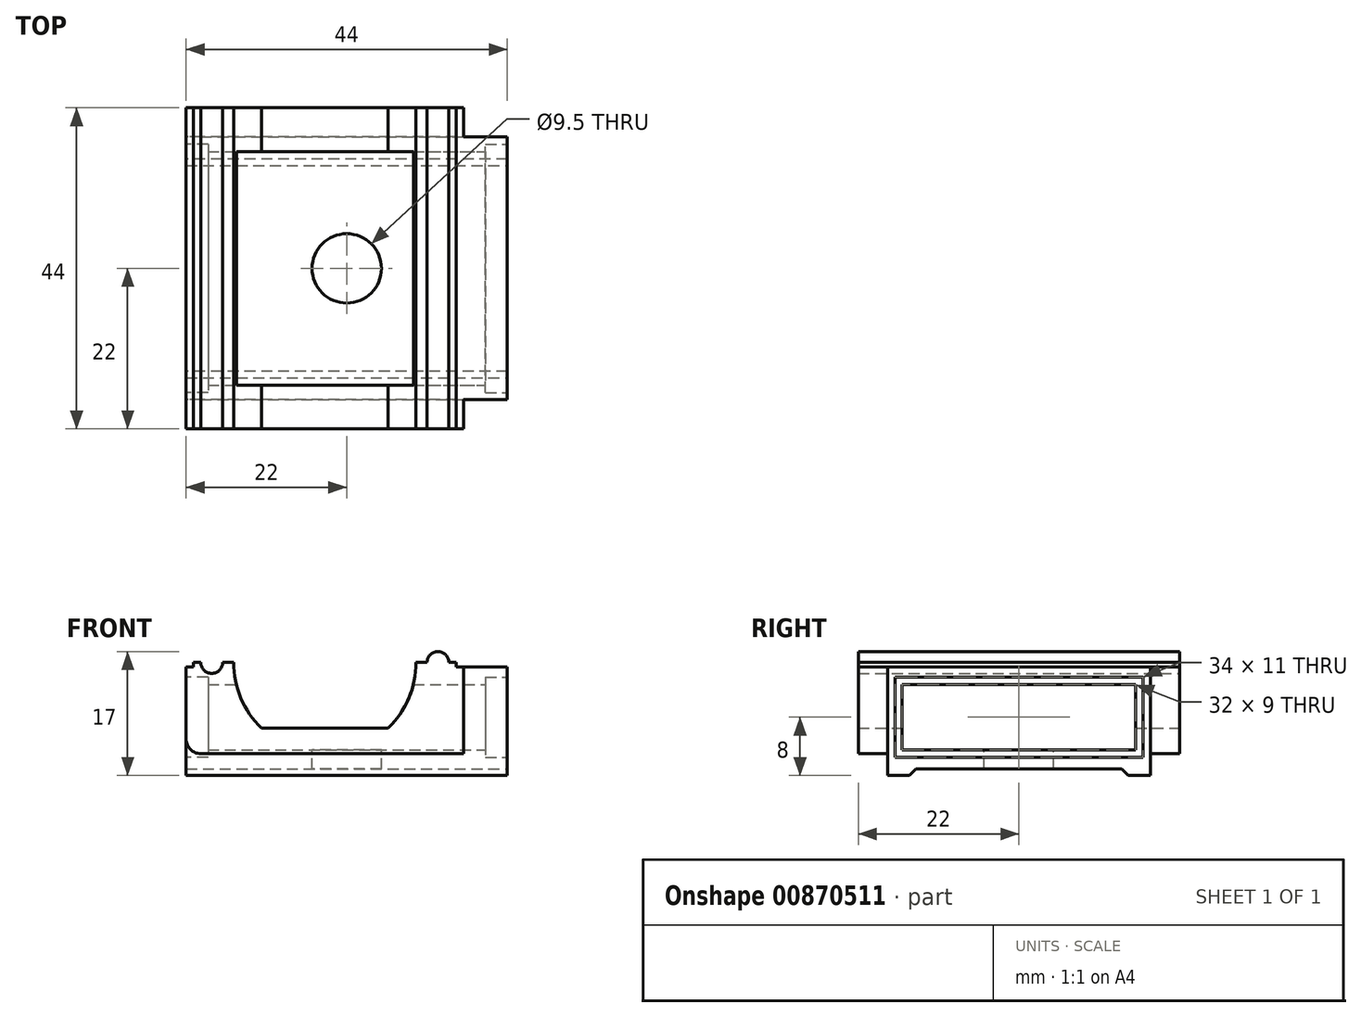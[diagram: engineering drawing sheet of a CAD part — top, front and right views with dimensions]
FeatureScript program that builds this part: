
annotation { "Feature Type Name" : "Feature", "Feature Type Description" : "" }
export const myFeature = defineFeature(function(context is Context, id is Id, definition is map)
    precondition{}
    {
        {
            var Q0;
            Q0=qCreatedBy(makeId("Top.planeOp"),FACE);
            var sketch = newSketch(context, id + "F0", { "sketchPlane" : qUnion([Q0])});
            skLineSegment(sketch, "E0.bottom", {"start": v(9.5, 19) * mm, "end": v(-9.5, 19) * mm});
            skLineSegment(sketch, "E0.top", {"start": v(9.5, -19) * mm, "end": v(-9.5, -19) * mm});
            skLineSegment(sketch, "E0.left", {"start": v(9.5, 19) * mm, "end": v(9.5, -19) * mm});
            skLineSegment(sketch, "E0.right", {"start": v(-9.5, 19) * mm, "end": v(-9.5, -19) * mm});
            skPoint(sketch, "E0.middle", {"position": v(0, 0) * mm});
            skLineSegment(sketch, "E1.bottom", {"start": v(-12.5, 22) * mm, "end": v(12.5, 22) * mm});
            skLineSegment(sketch, "E1.top", {"start": v(-12.5, -22) * mm, "end": v(12.5, -22) * mm});
            skLineSegment(sketch, "E1.left", {"start": v(-12.5, 22) * mm, "end": v(-12.5, -22) * mm});
            skLineSegment(sketch, "E1.right", {"start": v(12.5, 22) * mm, "end": v(12.5, -22) * mm});
            skCircle(sketch, "E2", {"center": v(3, 0) * mm, "radius": 4.75 * mm});
            skLineSegment(sketch, "E3.bottom", {"start": v(18.17, 25) * mm, "end": v(-18.17, 25) * mm});
            skLineSegment(sketch, "E3.top", {"start": v(18.17, -25) * mm, "end": v(-18.17, -25) * mm});
            skLineSegment(sketch, "E3.left", {"start": v(18.17, 25) * mm, "end": v(18.17, -25) * mm});
            skLineSegment(sketch, "E3.right", {"start": v(-18.17, 25) * mm, "end": v(-18.17, -25) * mm});
            skSolve(sketch);
        }
        {
            var Q0;
            Q0=qCreatedBy(makeId("Front.planeOp"),FACE);
            var sketch = newSketch(context, id + "F1", { "sketchPlane" : qUnion([Q0])});
            skCircle(sketch, "E4", {"center": v(0, 0) * mm, "radius": 9.5 * mm});
            skLineSegment(sketch, "E5.bottom", {"start": v(9.5, 6) * mm, "end": v(-9.5, 6) * mm});
            skLineSegment(sketch, "E5.top", {"start": v(9.5, -6) * mm, "end": v(-9.5, -6) * mm});
            skLineSegment(sketch, "E5.left", {"start": v(9.5, 6) * mm, "end": v(9.5, -6) * mm});
            skLineSegment(sketch, "E5.right", {"start": v(-9.5, 6) * mm, "end": v(-9.5, -6) * mm});
            skCircle(sketch, "E6", {"center": v(0, 0) * mm, "radius": 12.5 * mm});
            skLineSegment(sketch, "E7.bottom", {"start": v(-15.14, 9) * mm, "end": v(15.14, 9) * mm});
            skLineSegment(sketch, "E7.top", {"start": v(-15.14, -9) * mm, "end": v(15.14, -9) * mm});
            skLineSegment(sketch, "E7.left", {"start": v(-15.14, 9) * mm, "end": v(-15.14, -9) * mm});
            skLineSegment(sketch, "E7.right", {"start": v(15.14, 9) * mm, "end": v(15.14, -9) * mm});
            skLineSegment(sketch, "E8.bottom", {"start": v(-19, 12.6) * mm, "end": v(19, 12.6) * mm});
            skLineSegment(sketch, "E8.top", {"start": v(-19, -12.6) * mm, "end": v(19, -12.6) * mm});
            skLineSegment(sketch, "E8.left", {"start": v(-19, 12.6) * mm, "end": v(-19, -12.6) * mm});
            skLineSegment(sketch, "E8.right", {"start": v(19, 12.6) * mm, "end": v(19, -12.6) * mm});
            skCircle(sketch, "E9", {"center": v(0, 0) * mm, "radius": 15.5 * mm});
            skLineSegment(sketch, "E10", {"start": v(-15.14, 9) * mm, "end": v(-19, 9) * mm});
            skLineSegment(sketch, "E11", {"start": v(15.14, 9) * mm, "end": v(19, 9) * mm});
            skLineSegment(sketch, "E12", {"start": v(-15.14, -9) * mm, "end": v(-19, -9) * mm});
            skLineSegment(sketch, "E13", {"start": v(15.14, -9) * mm, "end": v(19, -9) * mm});
            skCircle(sketch, "E14", {"center": v(0, 0) * mm, "radius": 19 * mm});
            skLineSegment(sketch, "E15", {"start": v(-19, 0) * mm, "end": v(19, 0) * mm});
            skCircle(sketch, "E16", {"center": v(-15.5, 0) * mm, "radius": 1.5 * mm});
            skCircle(sketch, "E17", {"center": v(15.5, 0) * mm, "radius": 1.5 * mm});
            skLineSegment(sketch, "E18.bottom", {"start": v(-19, 0) * mm, "end": v(-18, 0) * mm});
            skLineSegment(sketch, "E18.top", {"start": v(-19, -0.6) * mm, "end": v(-18, -0.6) * mm});
            skLineSegment(sketch, "E18.left", {"start": v(-19, 0) * mm, "end": v(-19, -0.6) * mm});
            skLineSegment(sketch, "E18.right", {"start": v(-18, 0) * mm, "end": v(-18, -0.6) * mm});
            skLineSegment(sketch, "E19.bottom", {"start": v(19, 0) * mm, "end": v(18, 0) * mm});
            skLineSegment(sketch, "E19.top", {"start": v(19, -0.6) * mm, "end": v(18, -0.6) * mm});
            skLineSegment(sketch, "E19.left", {"start": v(19, 0) * mm, "end": v(19, -0.6) * mm});
            skLineSegment(sketch, "E19.right", {"start": v(18, 0) * mm, "end": v(18, -0.6) * mm});
            skLineSegment(sketch, "E20.top", {"start": v(-19, -14.6) * mm, "end": v(19, -14.6) * mm});
            skLineSegment(sketch, "E20.left", {"start": v(-19, -12.6) * mm, "end": v(-19, -14.6) * mm});
            skLineSegment(sketch, "E20.right", {"start": v(19, -12.6) * mm, "end": v(19, -14.6) * mm});
            skSolve(sketch);
        }
        {
            var Q0;
            Q0=qCreatedBy(makeId("Right.planeOp"),FACE);
            var sketch = newSketch(context, id + "F2", { "sketchPlane" : qUnion([Q0])});
            skLineSegment(sketch, "E21.bottom", {"start": v(-22, 12.5) * mm, "end": v(22, 12.5) * mm});
            skLineSegment(sketch, "E21.top", {"start": v(-22, -12.5) * mm, "end": v(22, -12.5) * mm});
            skLineSegment(sketch, "E21.left", {"start": v(-22, 12.5) * mm, "end": v(-22, -12.5) * mm});
            skLineSegment(sketch, "E21.right", {"start": v(22, 12.5) * mm, "end": v(22, -12.5) * mm});
            skPoint(sketch, "E21.middle", {"position": v(0, 0) * mm});
            skLineSegment(sketch, "E22.bottom", {"start": v(-18, -12.5) * mm, "end": v(-12, -12.5) * mm});
            skLineSegment(sketch, "E22.top", {"start": v(-18, -15.5) * mm, "end": v(-12, -15.5) * mm});
            skLineSegment(sketch, "E22.left", {"start": v(-18, -12.5) * mm, "end": v(-18, -15.5) * mm});
            skLineSegment(sketch, "E22.right", {"start": v(-12, -12.5) * mm, "end": v(-12, -15.5) * mm});
            skLineSegment(sketch, "E23.bottom", {"start": v(18, -12.5) * mm, "end": v(12, -12.5) * mm});
            skLineSegment(sketch, "E23.top", {"start": v(18, -15.5) * mm, "end": v(12, -15.5) * mm});
            skLineSegment(sketch, "E23.left", {"start": v(18, -12.5) * mm, "end": v(18, -15.5) * mm});
            skLineSegment(sketch, "E23.right", {"start": v(12, -12.5) * mm, "end": v(12, -15.5) * mm});
            skPoint(sketch, "E24.middle", {"position": v(0, -8.5) * mm});
            skLineSegment(sketch, "E25.bottom", {"start": v(18, -15.5) * mm, "end": v(22, -15.5) * mm});
            skLineSegment(sketch, "E25.top", {"start": v(18, -12.5) * mm, "end": v(22, -12.5) * mm});
            skLineSegment(sketch, "E25.left", {"start": v(18, -15.5) * mm, "end": v(18, -12.5) * mm});
            skLineSegment(sketch, "E25.right", {"start": v(22, -15.5) * mm, "end": v(22, -12.5) * mm});
            skLineSegment(sketch, "E26.bottom", {"start": v(-18, -15.5) * mm, "end": v(-22, -15.5) * mm});
            skLineSegment(sketch, "E26.top", {"start": v(-18, -12.5) * mm, "end": v(-22, -12.5) * mm});
            skLineSegment(sketch, "E26.left", {"start": v(-18, -15.5) * mm, "end": v(-18, -12.5) * mm});
            skLineSegment(sketch, "E26.right", {"start": v(-22, -15.5) * mm, "end": v(-22, -12.5) * mm});
            skSolve(sketch);
        }
        {
            var Q0;
            {var subQ4=sQuery(id+"F1.wireOp",EDGE,"E7.top");var subQ5=sQuery(id+"F1.wireOp",EDGE,"E6");var subQ6=makeQuery(id+"F1.imprint","INTERSECT",VERTEX,{"disambiguationData":[OD(0.0)],"derivedFrom":[subQ5,subQ4]});Q0=makeQuery(id+"F1.imprint","IMPRINT",FACE,{"disambiguationData":[TD([[makeQuery(id+"F1.imprint","IMPRINT",EDGE,{"disambiguationData":[TD([[subQ6,1.0]])],"derivedFrom":subQ5}),-1.0]])]});}
            var Q1;
            {var subQ0=sQuery(id+"F1.wireOp",EDGE,"E9");var subQ1=sQuery(id+"F1.wireOp",EDGE,"E7.top");var subQ2=makeQuery(id+"F1.imprint","INTERSECT",VERTEX,{"disambiguationData":[OD(0.0)],"derivedFrom":[subQ1,subQ0]});Q1=makeQuery(id+"F1.imprint","IMPRINT",FACE,{"disambiguationData":[TD([[makeQuery(id+"F1.imprint","IMPRINT",EDGE,{"disambiguationData":[TD([[subQ2,1.0]])],"derivedFrom":subQ0}),-1.0]])]});}
            var Q2;
            {var subQ0=sQuery(id+"F1.wireOp",EDGE,"E7.top");var subQ1=sQuery(id+"F1.wireOp",EDGE,"E4");var subQ2=makeQuery(id+"F1.imprint","INTERSECT",VERTEX,{"disambiguationData":[OD(0.0)],"derivedFrom":[subQ1,subQ0]});Q2=makeQuery(id+"F1.imprint","IMPRINT",FACE,{"disambiguationData":[TD([[makeQuery(id+"F1.imprint","IMPRINT",EDGE,{"disambiguationData":[TD([[subQ2,-1.0]])],"derivedFrom":subQ1}),-1.0]])]});}
            var Q3;
            {var subQ0=sQuery(id+"F1.wireOp",EDGE,"E7.right");var subQ3=sQuery(id+"F1.wireOp",EDGE,"E9");var subQ5=makeQuery(id+"F1.imprint","INTERSECT",VERTEX,{"disambiguationData":[OD(0.0)],"derivedFrom":[subQ0,subQ3]});Q3=makeQuery(id+"F1.imprint","IMPRINT",FACE,{"disambiguationData":[TD([[makeQuery(id+"F1.imprint","IMPRINT",EDGE,{"disambiguationData":[TD([[subQ5,1.0]])],"derivedFrom":subQ3}),-1.0]])]});}
            var Q4;
            {var subQ0=sQuery(id+"F1.wireOp",EDGE,"E8.right");var subQ1=sQuery(id+"F1.wireOp",EDGE,"E8.top");var subQ2=makeQuery(id+"F1.imprint","INTERSECT",VERTEX,{"derivedFrom":[subQ1,subQ0]});Q4=makeQuery(id+"F1.imprint","IMPRINT",FACE,{"disambiguationData":[TD([[makeQuery(id+"F1.imprint","IMPRINT",EDGE,{"disambiguationData":[TD([[subQ2,1.0]])],"derivedFrom":subQ1}),1.0]])]});}
            var Q5;
            {var subQ3=sQuery(id+"F1.wireOp",EDGE,"E14");var subQ7=sQuery(id+"F1.wireOp",EDGE,"E8.top");var subQ9=makeQuery(id+"F1.imprint","INTERSECT",VERTEX,{"disambiguationData":[OD(1.0)],"derivedFrom":[subQ7,subQ3]});Q5=makeQuery(id+"F1.imprint","IMPRINT",FACE,{"disambiguationData":[TD([[makeQuery(id+"F1.imprint","IMPRINT",EDGE,{"disambiguationData":[TD([[subQ9,1.0]])],"derivedFrom":subQ7}),1.0]])]});}
            var Q6;
            {var subQ3=sQuery(id+"F1.wireOp",EDGE,"E14");var subQ7=sQuery(id+"F1.wireOp",EDGE,"E8.top");var subQ9=makeQuery(id+"F1.imprint","INTERSECT",VERTEX,{"disambiguationData":[OD(0.0)],"derivedFrom":[subQ7,subQ3]});Q6=makeQuery(id+"F1.imprint","IMPRINT",FACE,{"disambiguationData":[TD([[makeQuery(id+"F1.imprint","IMPRINT",EDGE,{"disambiguationData":[TD([[subQ9,-1.0]])],"derivedFrom":subQ7}),1.0]])]});}
            var Q7;
            {var subQ0=sQuery(id+"F1.wireOp",EDGE,"E8.left");var subQ1=sQuery(id+"F1.wireOp",EDGE,"E8.top");var subQ2=makeQuery(id+"F1.imprint","INTERSECT",VERTEX,{"derivedFrom":[subQ1,subQ0]});Q7=makeQuery(id+"F1.imprint","IMPRINT",FACE,{"disambiguationData":[TD([[makeQuery(id+"F1.imprint","IMPRINT",EDGE,{"disambiguationData":[TD([[subQ2,-1.0]])],"derivedFrom":subQ1}),1.0]])]});}
            var Q8;
            {var subQ5=sQuery(id+"F1.wireOp",EDGE,"E18.right");Q8=makeQuery(id+"F1.imprint","IMPRINT",FACE,{"disambiguationData":[TD([[makeQuery(id+"F1.imprint","IMPRINT",EDGE,{"derivedFrom":subQ5}),1.0]])]});}
            var Q9;
            {var subQ7=sQuery(id+"F1.wireOp",EDGE,"E15");var subQ8=sQuery(id+"F1.wireOp",EDGE,"E6");var subQ9=makeQuery(id+"F1.imprint","INTERSECT",VERTEX,{"disambiguationData":[OD(1.0)],"derivedFrom":[subQ8,subQ7]});Q9=makeQuery(id+"F1.imprint","IMPRINT",FACE,{"disambiguationData":[TD([[makeQuery(id+"F1.imprint","IMPRINT",EDGE,{"disambiguationData":[TD([[subQ9,-1.0]])],"derivedFrom":subQ8}),-1.0]])]});}
            var Q10;
            {var subQ7=sQuery(id+"F1.wireOp",EDGE,"E6");var subQ9=sQuery(id+"F1.wireOp",EDGE,"E15");var subQ10=makeQuery(id+"F1.imprint","INTERSECT",VERTEX,{"disambiguationData":[OD(0.0)],"derivedFrom":[subQ7,subQ9]});Q10=makeQuery(id+"F1.imprint","IMPRINT",FACE,{"disambiguationData":[TD([[makeQuery(id+"F1.imprint","IMPRINT",EDGE,{"disambiguationData":[TD([[subQ10,1.0]])],"derivedFrom":subQ7}),-1.0]])]});}
            var Q11;
            {var subQ5=sQuery(id+"F1.wireOp",EDGE,"E19.right");Q11=makeQuery(id+"F1.imprint","IMPRINT",FACE,{"disambiguationData":[TD([[makeQuery(id+"F1.imprint","IMPRINT",EDGE,{"derivedFrom":subQ5}),-1.0]])]});}
            var Q12;
            {var subQ0=sQuery(id+"F1.wireOp",EDGE,"E17");var subQ1=sQuery(id+"F1.wireOp",EDGE,"E7.right");var subQ2=makeQuery(id+"F1.imprint","INTERSECT",VERTEX,{"disambiguationData":[OD(0.0)],"derivedFrom":[subQ1,subQ0]});Q12=makeQuery(id+"F1.imprint","IMPRINT",FACE,{"disambiguationData":[TD([[makeQuery(id+"F1.imprint","IMPRINT",EDGE,{"disambiguationData":[TD([[subQ2,1.0]])],"derivedFrom":subQ1}),1.0]])]});}
            var Q13;
            {var subQ0=sQuery(id+"F1.wireOp",EDGE,"E9");var subQ1=sQuery(id+"F1.wireOp",EDGE,"E7.left");var subQ2=makeQuery(id+"F1.imprint","INTERSECT",VERTEX,{"disambiguationData":[OD(1.0)],"derivedFrom":[subQ1,subQ0]});Q13=makeQuery(id+"F1.imprint","IMPRINT",FACE,{"disambiguationData":[TD([[makeQuery(id+"F1.imprint","IMPRINT",EDGE,{"disambiguationData":[TD([[subQ2,1.0]])],"derivedFrom":subQ1}),-1.0]])]});}
            var Q14;
            {var subQ0=sQuery(id+"F1.wireOp",EDGE,"E9");var subQ1=sQuery(id+"F1.wireOp",EDGE,"E7.right");var subQ2=makeQuery(id+"F1.imprint","INTERSECT",VERTEX,{"disambiguationData":[OD(0.0)],"derivedFrom":[subQ1,subQ0]});Q14=makeQuery(id+"F1.imprint","IMPRINT",FACE,{"disambiguationData":[TD([[makeQuery(id+"F1.imprint","IMPRINT",EDGE,{"disambiguationData":[TD([[subQ2,1.0]])],"derivedFrom":subQ1}),1.0]])]});}
            var Q15;
            {var subQ0=sQuery(id+"F1.wireOp",EDGE,"E17");var subQ1=sQuery(id+"F1.wireOp",EDGE,"E7.right");var subQ2=makeQuery(id+"F1.imprint","INTERSECT",VERTEX,{"disambiguationData":[OD(0.0)],"derivedFrom":[subQ1,subQ0]});Q15=makeQuery(id+"F1.imprint","IMPRINT",FACE,{"disambiguationData":[TD([[makeQuery(id+"F1.imprint","IMPRINT",EDGE,{"disambiguationData":[TD([[subQ2,1.0]])],"derivedFrom":subQ1}),-1.0]])]});}
            var Q16;
            {var subQ0=sQuery(id+"F1.wireOp",EDGE,"E15");var subQ1=sQuery(id+"F1.wireOp",EDGE,"E9");var subQ2=makeQuery(id+"F1.imprint","INTERSECT",VERTEX,{"disambiguationData":[OD(0.0)],"derivedFrom":[subQ1,subQ0]});Q16=makeQuery(id+"F1.imprint","IMPRINT",FACE,{"disambiguationData":[TD([[makeQuery(id+"F1.imprint","IMPRINT",EDGE,{"disambiguationData":[TD([[subQ2,1.0]])],"derivedFrom":subQ1}),-1.0]])]});}
            var Q17;
            {var subQ0=sQuery(id+"F1.wireOp",EDGE,"E15");var subQ1=sQuery(id+"F1.wireOp",EDGE,"E9");var subQ2=makeQuery(id+"F1.imprint","INTERSECT",VERTEX,{"disambiguationData":[OD(0.0)],"derivedFrom":[subQ1,subQ0]});Q17=makeQuery(id+"F1.imprint","IMPRINT",FACE,{"disambiguationData":[TD([[makeQuery(id+"F1.imprint","IMPRINT",EDGE,{"disambiguationData":[TD([[subQ2,-1.0]])],"derivedFrom":subQ1}),-1.0]])]});}
            var Q18;
            {var subQ0=sQuery(id+"F1.wireOp",EDGE,"E17");var subQ1=sQuery(id+"F1.wireOp",EDGE,"E7.right");var subQ2=makeQuery(id+"F1.imprint","INTERSECT",VERTEX,{"disambiguationData":[OD(1.0)],"derivedFrom":[subQ1,subQ0]});Q18=makeQuery(id+"F1.imprint","IMPRINT",FACE,{"disambiguationData":[TD([[makeQuery(id+"F1.imprint","IMPRINT",EDGE,{"disambiguationData":[TD([[subQ2,-1.0]])],"derivedFrom":subQ1}),1.0]])]});}
            var Q19;
            {var subQ0=sQuery(id+"F1.wireOp",EDGE,"E17");var subQ1=sQuery(id+"F1.wireOp",EDGE,"E7.right");var subQ2=makeQuery(id+"F1.imprint","INTERSECT",VERTEX,{"disambiguationData":[OD(1.0)],"derivedFrom":[subQ1,subQ0]});Q19=makeQuery(id+"F1.imprint","IMPRINT",FACE,{"disambiguationData":[TD([[makeQuery(id+"F1.imprint","IMPRINT",EDGE,{"disambiguationData":[TD([[subQ2,-1.0]])],"derivedFrom":subQ1}),-1.0]])]});}
            var Q20;
            {var subQ0=sQuery(id+"F1.wireOp",EDGE,"E7.top");var subQ1=sQuery(id+"F1.wireOp",EDGE,"E4");var subQ2=makeQuery(id+"F1.imprint","INTERSECT",VERTEX,{"disambiguationData":[OD(0.0)],"derivedFrom":[subQ1,subQ0]});Q20=makeQuery(id+"F1.imprint","IMPRINT",FACE,{"disambiguationData":[TD([[makeQuery(id+"F1.imprint","IMPRINT",EDGE,{"disambiguationData":[TD([[subQ2,-1.0]])],"derivedFrom":subQ1}),1.0]])]});}
            var Q21;
            {var subQ0=sQuery(id+"F1.wireOp",EDGE,"E18.top");var subQ1=sQuery(id+"F1.wireOp",EDGE,"E8.left");var subQ2=makeQuery(id+"F1.imprint","INTERSECT",VERTEX,{"derivedFrom":[subQ1,subQ0]});Q21=makeQuery(id+"F1.imprint","IMPRINT",FACE,{"disambiguationData":[TD([[makeQuery(id+"F1.imprint","IMPRINT",EDGE,{"disambiguationData":[TD([[subQ2,-1.0]])],"derivedFrom":subQ1}),1.0]])]});}
            var Q22;
            {var subQ0=sQuery(id+"F1.wireOp",EDGE,"E19.top");var subQ1=sQuery(id+"F1.wireOp",EDGE,"E8.right");var subQ2=makeQuery(id+"F1.imprint","INTERSECT",VERTEX,{"derivedFrom":[subQ1,subQ0]});Q22=makeQuery(id+"F1.imprint","IMPRINT",FACE,{"disambiguationData":[TD([[makeQuery(id+"F1.imprint","IMPRINT",EDGE,{"disambiguationData":[TD([[subQ2,-1.0]])],"derivedFrom":subQ1}),-1.0]])]});}
            var Q23;
            {var subQ5=sQuery(id+"F1.wireOp",EDGE,"E9");var subQ6=sQuery(id+"F1.wireOp",EDGE,"E8.top");var subQ7=makeQuery(id+"F1.imprint","INTERSECT",VERTEX,{"disambiguationData":[OD(0.0)],"derivedFrom":[subQ6,subQ5]});Q23=makeQuery(id+"F1.imprint","IMPRINT",FACE,{"disambiguationData":[TD([[makeQuery(id+"F1.imprint","IMPRINT",EDGE,{"disambiguationData":[TD([[subQ7,1.0]])],"derivedFrom":subQ6}),1.0]])]});}
            var Q24;
            {var subQ0=sQuery(id+"F1.wireOp",EDGE,"E14");var subQ5=sQuery(id+"F1.wireOp",EDGE,"E12");var subQ6=makeQuery(id+"F1.imprint","INTERSECT",VERTEX,{"derivedFrom":[subQ5,subQ0]});Q24=makeQuery(id+"F1.imprint","IMPRINT",FACE,{"disambiguationData":[TD([[makeQuery(id+"F1.imprint","IMPRINT",EDGE,{"disambiguationData":[TD([[subQ6,-1.0]])],"derivedFrom":subQ5}),1.0]])]});}
            var Q25;
            {var subQ5=sQuery(id+"F1.wireOp",EDGE,"E9");var subQ6=sQuery(id+"F1.wireOp",EDGE,"E8.top");var subQ7=makeQuery(id+"F1.imprint","INTERSECT",VERTEX,{"disambiguationData":[OD(1.0)],"derivedFrom":[subQ6,subQ5]});Q25=makeQuery(id+"F1.imprint","IMPRINT",FACE,{"disambiguationData":[TD([[makeQuery(id+"F1.imprint","IMPRINT",EDGE,{"disambiguationData":[TD([[subQ7,-1.0]])],"derivedFrom":subQ6}),1.0]])]});}
            var Q26;
            {var subQ3=sQuery(id+"F1.wireOp",EDGE,"E14");var subQ5=sQuery(id+"F1.wireOp",EDGE,"E13");var subQ7=makeQuery(id+"F1.imprint","INTERSECT",VERTEX,{"derivedFrom":[subQ5,subQ3]});Q26=makeQuery(id+"F1.imprint","IMPRINT",FACE,{"disambiguationData":[TD([[makeQuery(id+"F1.imprint","IMPRINT",EDGE,{"disambiguationData":[TD([[subQ7,-1.0]])],"derivedFrom":subQ5}),-1.0]])]});}
            var Q27;
            {var subQ3=sQuery(id+"F1.wireOp",EDGE,"E20.left");Q27=makeQuery(id+"F1.imprint","IMPRINT",FACE,{"disambiguationData":[TD([[makeQuery(id+"F1.imprint","IMPRINT",EDGE,{"derivedFrom":subQ3}),1.0]])]});}
            var Q28;
            {var subQ0=sQuery(id+"F1.wireOp",EDGE,"E9");var subQ1=sQuery(id+"F1.wireOp",EDGE,"E8.top");var subQ2=makeQuery(id+"F1.imprint","INTERSECT",VERTEX,{"disambiguationData":[OD(0.0)],"derivedFrom":[subQ1,subQ0]});Q28=makeQuery(id+"F1.imprint","IMPRINT",FACE,{"disambiguationData":[TD([[makeQuery(id+"F1.imprint","IMPRINT",EDGE,{"disambiguationData":[TD([[subQ2,1.0]])],"derivedFrom":subQ1}),-1.0]])]});}
            var Q29;
            {var subQ0=sQuery(id+"F1.wireOp",EDGE,"E9");var subQ1=sQuery(id+"F1.wireOp",EDGE,"E8.top");var subQ2=makeQuery(id+"F1.imprint","INTERSECT",VERTEX,{"disambiguationData":[OD(0.0)],"derivedFrom":[subQ1,subQ0]});Q29=makeQuery(id+"F1.imprint","IMPRINT",FACE,{"disambiguationData":[TD([[makeQuery(id+"F1.imprint","IMPRINT",EDGE,{"disambiguationData":[TD([[subQ2,-1.0]])],"derivedFrom":subQ1}),-1.0]])]});}
            var Q30;
            {var subQ0=sQuery(id+"F1.wireOp",EDGE,"E20.right");Q30=makeQuery(id+"F1.imprint","IMPRINT",FACE,{"disambiguationData":[TD([[makeQuery(id+"F1.imprint","IMPRINT",EDGE,{"derivedFrom":subQ0}),-1.0]])]});}
            var Q31;
            {var subQ0=sQuery(id+"F1.wireOp",EDGE,"E9");var subQ1=sQuery(id+"F1.wireOp",EDGE,"E8.top");var subQ2=makeQuery(id+"F1.imprint","INTERSECT",VERTEX,{"disambiguationData":[OD(1.0)],"derivedFrom":[subQ1,subQ0]});Q31=makeQuery(id+"F1.imprint","IMPRINT",FACE,{"disambiguationData":[TD([[makeQuery(id+"F1.imprint","IMPRINT",EDGE,{"disambiguationData":[TD([[subQ2,-1.0]])],"derivedFrom":subQ1}),-1.0]])]});}
            extrude(context, id + "F3", {"entities" : qUnion([Q0, Q1, Q2, Q3, Q4, Q5, Q6, Q7, Q8, Q9, Q10, Q11, Q12, Q13, Q14, Q15, Q16, Q17, Q18, Q19, Q20, Q21, Q22, Q23, Q24, Q25, Q26, Q27, Q28, Q29, Q30, Q31]), "endBound" : BoundingType.SYMMETRIC, "depth" : 44 * mm, "offsetDistance" : 25 * mm});
        }
        {
            var Q0;
            Q0=makeQuery(id+"F0.imprint","IMPRINT",FACE,{"disambiguationData":[TD([[makeQuery(id+"F0.imprint","IMPRINT",EDGE,{"derivedFrom":sQuery(id+"F0.wireOp",EDGE,"E2")}),1.0]])]});
            extrude(context, id + "F4", {"entities" : qUnion([Q0]), "operationType" : NewBodyOperationType.REMOVE, "oppositeDirection" : true, "depth" : 25 * mm, "offsetDistance" : 25 * mm});
        }
        {
            var Q0;
            Q0=makeQuery(id+"F2.imprint","IMPRINT",FACE,{"disambiguationData":[TD([[makeQuery(id+"F2.imprint","IMPRINT",EDGE,{"derivedFrom":sQuery(id+"F2.wireOp",EDGE,"E22.top")}),1.0]])]});
            var Q1;
            Q1=makeQuery(id+"F2.imprint","IMPRINT",FACE,{"disambiguationData":[TD([[makeQuery(id+"F2.imprint","IMPRINT",EDGE,{"derivedFrom":sQuery(id+"F2.wireOp",EDGE,"E23.top")}),-1.0]])]});
            extrude(context, id + "F5", {"entities" : qUnion([Q0, Q1]), "operationType" : NewBodyOperationType.ADD, "endBound" : BoundingType.SYMMETRIC, "depth" : 38 * mm, "offsetDistance" : 25 * mm});
        }
        {
            var Q0;
            Q0=makeQuery(id+"F3.opExtrude","SWEPT_FACE",FACE,{"disambiguationData":[OSD([sQuery(id+"F1.wireOp",EDGE,"E7.top")])]});
            var sketch = newSketch(context, id + "F6", { "sketchPlane" : qUnion([Q0])});
            skLineSegment(sketch, "E27.bottom", {"start": v(-27, 16) * mm, "end": v(33, 16) * mm});
            skLineSegment(sketch, "E27.top", {"start": v(-27, -16) * mm, "end": v(33, -16) * mm});
            skLineSegment(sketch, "E27.left", {"start": v(-27, 16) * mm, "end": v(-27, -16) * mm});
            skLineSegment(sketch, "E27.right", {"start": v(33, 16) * mm, "end": v(33, -16) * mm});
            skPoint(sketch, "E27.middle", {"position": v(3, 0) * mm});
            skSolve(sketch);
        }
        {
            var Q0;
            Q0 = qSketchRegion(id + "F6", true);
            extrude(context, id + "F7", {"entities" : qUnion([Q0]), "operationType" : NewBodyOperationType.REMOVE, "oppositeDirection" : true, "depth" : 3 * mm, "offsetDistance" : 25 * mm});
        }
        {
            var Q0;
            Q0 = qSketchRegion(id + "F6", true);
            extrude(context, id + "F8", {"entities" : qUnion([Q0]), "operationType" : NewBodyOperationType.REMOVE, "depth" : 3 * mm, "offsetDistance" : 25 * mm});
        }
        {
            var Q0;
            {var subQ2=sQuery(id+"F6.wireOp",EDGE,"E27.bottom");var subQ3=sQuery(id+"F6.wireOp",EDGE,"E27.top");Q0=makeQuery(id+"F8.boolean.opBoolean","COPY",FACE,{"disambiguationData":[TD([makeQuery(id+"F3.opExtrude","SWEPT_FACE",FACE,{"disambiguationData":[OSD([sQuery(id+"F1.wireOp",EDGE,"E8.left"),sQuery(id+"F1.wireOp",EDGE,"E20.left")])]})])],"derivedFrom":makeQuery(id+"F8.opExtrude","CAP_FACE",FACE,{"disambiguationData":[OSD([subQ2,subQ3,sQuery(id+"F6.wireOp",EDGE,"E27.left"),sQuery(id+"F6.wireOp",EDGE,"E27.right")])],"isStart":false})});}
            extrude(context, id + "F9", {"entities" : qUnion([Q0]), "operationType" : NewBodyOperationType.REMOVE, "oppositeDirection" : true, "depth" : 3 * mm, "offsetDistance" : 25 * mm});
        }
        {
            var Q0;
            {var subQ1=sQuery(id+"F6.wireOp",EDGE,"E27.top");var subQ2=sQuery(id+"F6.wireOp",EDGE,"E27.bottom");Q0=makeQuery(id+"F8.boolean.opBoolean","COPY",FACE,{"disambiguationData":[TD([makeQuery(id+"F3.opExtrude","SWEPT_FACE",FACE,{"disambiguationData":[OSD([sQuery(id+"F1.wireOp",EDGE,"E8.right"),sQuery(id+"F1.wireOp",EDGE,"E20.right")])]})])],"derivedFrom":makeQuery(id+"F8.opExtrude","CAP_FACE",FACE,{"disambiguationData":[OSD([subQ2,subQ1,sQuery(id+"F6.wireOp",EDGE,"E27.left"),sQuery(id+"F6.wireOp",EDGE,"E27.right")])],"isStart":false})});}
            extrude(context, id + "F10", {"entities" : qUnion([Q0]), "operationType" : NewBodyOperationType.REMOVE, "oppositeDirection" : true, "depth" : 3 * mm, "offsetDistance" : 25 * mm});
        }
        {
            var Q0;
            {var subQ0=sQuery(id+"F2.wireOp",EDGE,"E21.top");Q0=makeQuery(id+"F5.boolean.opBoolean","MERGE",FACE,{"derivedFrom":[makeQuery(id+"F3.opExtrude","SWEPT_FACE",FACE,{"disambiguationData":[OSD([sQuery(id+"F1.wireOp",EDGE,"E8.right"),sQuery(id+"F1.wireOp",EDGE,"E20.right")])]}),makeQuery(id+"F5.opExtrude","CAP_FACE",FACE,{"disambiguationData":[OSD([subQ0,sQuery(id+"F2.wireOp",EDGE,"E23.top"),sQuery(id+"F2.wireOp",EDGE,"E23.left"),sQuery(id+"F2.wireOp",EDGE,"E23.right")])],"isStart":false}),makeQuery(id+"F5.opExtrude","CAP_FACE",FACE,{"disambiguationData":[OSD([subQ0,sQuery(id+"F2.wireOp",EDGE,"E22.top"),sQuery(id+"F2.wireOp",EDGE,"E22.left"),sQuery(id+"F2.wireOp",EDGE,"E22.right")])],"isStart":false})]});}
            extrude(context, id + "F11", {"entities" : qUnion([Q0]), "operationType" : NewBodyOperationType.ADD, "depth" : 6 * mm, "offsetDistance" : 25 * mm});
        }
        {
            var Q0;
            Q0=makeQuery(id+"F11.opExtrude","CAP_FACE",FACE,{"disambiguationData":[OSD([sQuery(id+"F1.wireOp",EDGE,"E8.right"),sQuery(id+"F1.wireOp",EDGE,"E20.right"),sQuery(id+"F2.wireOp",EDGE,"E21.top"),sQuery(id+"F2.wireOp",EDGE,"E22.top"),sQuery(id+"F2.wireOp",EDGE,"E22.left"),sQuery(id+"F2.wireOp",EDGE,"E22.right"),sQuery(id+"F2.wireOp",EDGE,"E23.top"),sQuery(id+"F2.wireOp",EDGE,"E23.left"),sQuery(id+"F2.wireOp",EDGE,"E23.right")])],"isStart":false});
            var sketch = newSketch(context, id + "F12", { "sketchPlane" : qUnion([Q0])});
            skLineSegment(sketch, "E28.bottom", {"start": v(-17, -2) * mm, "end": v(17, -2) * mm});
            skLineSegment(sketch, "E28.top", {"start": v(-17, -13) * mm, "end": v(17, -13) * mm});
            skLineSegment(sketch, "E28.left", {"start": v(-17, -2) * mm, "end": v(-17, -13) * mm});
            skLineSegment(sketch, "E28.right", {"start": v(17, -2) * mm, "end": v(17, -13) * mm});
            skSolve(sketch);
        }
        {
            var Q0;
            Q0=makeQuery(id+"F12.imprint","IMPRINT",FACE,{"disambiguationData":[TD([[makeQuery(id+"F12.imprint","IMPRINT",EDGE,{"derivedFrom":sQuery(id+"F12.wireOp",EDGE,"E28.bottom")}),-1.0]])]});
            extrude(context, id + "F13", {"entities" : qUnion([Q0]), "operationType" : NewBodyOperationType.REMOVE, "oppositeDirection" : true, "depth" : 3 * mm, "offsetDistance" : 25 * mm});
        }
        {
            var Q0;
            {var subQ0=sQuery(id+"F2.wireOp",EDGE,"E21.top");Q0=makeQuery(id+"F5.boolean.opBoolean","MERGE",FACE,{"derivedFrom":[makeQuery(id+"F3.opExtrude","SWEPT_FACE",FACE,{"disambiguationData":[OSD([sQuery(id+"F1.wireOp",EDGE,"E8.left"),sQuery(id+"F1.wireOp",EDGE,"E20.left")])]}),makeQuery(id+"F5.opExtrude","CAP_FACE",FACE,{"disambiguationData":[OSD([subQ0,sQuery(id+"F2.wireOp",EDGE,"E23.top"),sQuery(id+"F2.wireOp",EDGE,"E23.left"),sQuery(id+"F2.wireOp",EDGE,"E23.right")])],"isStart":true}),makeQuery(id+"F5.opExtrude","CAP_FACE",FACE,{"disambiguationData":[OSD([subQ0,sQuery(id+"F2.wireOp",EDGE,"E22.top"),sQuery(id+"F2.wireOp",EDGE,"E22.left"),sQuery(id+"F2.wireOp",EDGE,"E22.right")])],"isStart":true})]});}
            var sketch = newSketch(context, id + "F14", { "sketchPlane" : qUnion([Q0])});
            skLineSegment(sketch, "E29.bottom", {"start": v(-17, -2) * mm, "end": v(17, -2) * mm});
            skLineSegment(sketch, "E29.top", {"start": v(-17, -13) * mm, "end": v(17, -13) * mm});
            skLineSegment(sketch, "E29.left", {"start": v(-17, -2) * mm, "end": v(-17, -13) * mm});
            skLineSegment(sketch, "E29.right", {"start": v(17, -2) * mm, "end": v(17, -13) * mm});
            skSolve(sketch);
        }
        {
            var Q0;
            Q0=makeQuery(id+"F14.imprint","IMPRINT",FACE,{"disambiguationData":[TD([[makeQuery(id+"F14.imprint","IMPRINT",EDGE,{"derivedFrom":sQuery(id+"F14.wireOp",EDGE,"E29.bottom")}),-1.0]])]});
            extrude(context, id + "F15", {"entities" : qUnion([Q0]), "operationType" : NewBodyOperationType.REMOVE, "oppositeDirection" : true, "depth" : 3 * mm, "offsetDistance" : 25 * mm});
        }
        {
            var Q0;
            {var subQ2=sQuery(id+"F2.wireOp",EDGE,"E23.left");Q0=makeQuery(id+"F2.imprint","IMPRINT",FACE,{"disambiguationData":[TD([[makeQuery(id+"F2.imprint","IMPRINT",EDGE,{"derivedFrom":subQ2}),1.0]])]});}
            var Q1;
            {var subQ0=sQuery(id+"F2.wireOp",EDGE,"E22.left");Q1=makeQuery(id+"F2.imprint","IMPRINT",FACE,{"disambiguationData":[TD([[makeQuery(id+"F2.imprint","IMPRINT",EDGE,{"derivedFrom":subQ0}),-1.0]])]});}
            extrude(context, id + "F16", {"entities" : qUnion([Q0, Q1]), "operationType" : NewBodyOperationType.REMOVE, "endBound" : BoundingType.SYMMETRIC, "oppositeDirection" : true, "depth" : 50 * mm, "offsetDistance" : 25 * mm});
        }
        {
            var Q0;
            {var subQ0=sQuery(id+"F2.wireOp",EDGE,"E23.right");var subQ1=sQuery(id+"F2.wireOp",EDGE,"E23.top");Q0=makeQuery(id+"F11.boolean.opBoolean","MERGE",EDGE,{"derivedFrom":[makeQuery(id+"F5.opExtrude","SWEPT_EDGE",EDGE,{"disambiguationData":[OSD([subQ1,subQ0])]}),makeQuery(id+"F11.opExtrude","SWEPT_EDGE",EDGE,{"disambiguationData":[OSD([subQ1,subQ0])]})]});}
            var Q1;
            {var subQ0=sQuery(id+"F2.wireOp",EDGE,"E22.right");var subQ1=sQuery(id+"F2.wireOp",EDGE,"E22.top");Q1=makeQuery(id+"F11.boolean.opBoolean","MERGE",EDGE,{"derivedFrom":[makeQuery(id+"F5.opExtrude","SWEPT_EDGE",EDGE,{"disambiguationData":[OSD([subQ1,subQ0])]}),makeQuery(id+"F11.opExtrude","SWEPT_EDGE",EDGE,{"disambiguationData":[OSD([subQ1,subQ0])]})]});}
            chamfer(context, id + "F17", {"entities" : qUnion([Q0, Q1]), "width" : 3 * mm, "tangentPropagation" : true});
        }
        {
            var Q0;
            {var subQ0=sQuery(id+"F1.wireOp",EDGE,"E20.right");var subQ1=sQuery(id+"F1.wireOp",EDGE,"E8.right");Q0=makeQuery(id+"F11.boolean.opBoolean","MERGE",FACE,{"derivedFrom":[makeQuery(id+"F3.opExtrude","CAP_FACE",FACE,{"disambiguationData":[OSD([sQuery(id+"F1.wireOp",EDGE,"E6"),sQuery(id+"F1.wireOp",EDGE,"E7.top"),sQuery(id+"F1.wireOp",EDGE,"E8.left"),subQ1,sQuery(id+"F1.wireOp",EDGE,"E15"),sQuery(id+"F1.wireOp",EDGE,"E16"),sQuery(id+"F1.wireOp",EDGE,"E17"),sQuery(id+"F1.wireOp",EDGE,"E18.top"),sQuery(id+"F1.wireOp",EDGE,"E18.right"),sQuery(id+"F1.wireOp",EDGE,"E19.top"),sQuery(id+"F1.wireOp",EDGE,"E19.right"),sQuery(id+"F1.wireOp",EDGE,"E20.top"),sQuery(id+"F1.wireOp",EDGE,"E20.left"),subQ0])],"isStart":false}),makeQuery(id+"F11.opExtrude","SWEPT_FACE",FACE,{"disambiguationData":[OSD([subQ1,subQ0]),TDD([makeQuery(id+"F3.opExtrude","CAP_EDGE",EDGE,{"disambiguationData":[OSD([subQ1,subQ0])],"isStart":false})])]})]});}
            var sketch = newSketch(context, id + "F18", { "sketchPlane" : qUnion([Q0])});
            skLineSegment(sketch, "E30.bottom", {"start": v(25, -12.5) * mm, "end": v(19, -12.5) * mm});
            skLineSegment(sketch, "E30.top", {"start": v(25, -0.6) * mm, "end": v(19, -0.6) * mm});
            skLineSegment(sketch, "E30.left", {"start": v(25, -12.5) * mm, "end": v(25, -0.6) * mm});
            skLineSegment(sketch, "E30.right", {"start": v(19, -12.5) * mm, "end": v(19, -0.6) * mm});
            skSolve(sketch);
        }
        {
            var Q0;
            Q0=makeQuery(id+"F18.imprint","IMPRINT",FACE,{"disambiguationData":[TD([[makeQuery(id+"F18.imprint","IMPRINT",EDGE,{"derivedFrom":sQuery(id+"F18.wireOp",EDGE,"E30.bottom")}),1.0]])]});
            extrude(context, id + "F19", {"entities" : qUnion([Q0]), "operationType" : NewBodyOperationType.REMOVE, "oppositeDirection" : true, "depth" : 4 * mm, "offsetDistance" : 25 * mm});
        }
        {
            var Q0;
            {var subQ0=sQuery(id+"F1.wireOp",EDGE,"E20.right");var subQ1=sQuery(id+"F1.wireOp",EDGE,"E8.right");Q0=makeQuery(id+"F11.boolean.opBoolean","MERGE",FACE,{"derivedFrom":[makeQuery(id+"F3.opExtrude","CAP_FACE",FACE,{"disambiguationData":[OSD([sQuery(id+"F1.wireOp",EDGE,"E6"),sQuery(id+"F1.wireOp",EDGE,"E7.top"),sQuery(id+"F1.wireOp",EDGE,"E8.left"),subQ1,sQuery(id+"F1.wireOp",EDGE,"E15"),sQuery(id+"F1.wireOp",EDGE,"E16"),sQuery(id+"F1.wireOp",EDGE,"E17"),sQuery(id+"F1.wireOp",EDGE,"E18.top"),sQuery(id+"F1.wireOp",EDGE,"E18.right"),sQuery(id+"F1.wireOp",EDGE,"E19.top"),sQuery(id+"F1.wireOp",EDGE,"E19.right"),sQuery(id+"F1.wireOp",EDGE,"E20.top"),sQuery(id+"F1.wireOp",EDGE,"E20.left"),subQ0])],"isStart":true}),makeQuery(id+"F11.opExtrude","SWEPT_FACE",FACE,{"disambiguationData":[OSD([subQ1,subQ0]),TDD([makeQuery(id+"F3.opExtrude","CAP_EDGE",EDGE,{"disambiguationData":[OSD([subQ1,subQ0])],"isStart":true})])]})]});}
            var sketch = newSketch(context, id + "F20", { "sketchPlane" : qUnion([Q0])});
            skLineSegment(sketch, "E31.bottom", {"start": v(-25, -12.5) * mm, "end": v(-19, -12.5) * mm});
            skLineSegment(sketch, "E31.top", {"start": v(-25, -0.6) * mm, "end": v(-19, -0.6) * mm});
            skLineSegment(sketch, "E31.left", {"start": v(-25, -12.5) * mm, "end": v(-25, -0.6) * mm});
            skLineSegment(sketch, "E31.right", {"start": v(-19, -12.5) * mm, "end": v(-19, -0.6) * mm});
            skSolve(sketch);
        }
        {
            var Q0;
            Q0=makeQuery(id+"F20.imprint","IMPRINT",FACE,{"disambiguationData":[TD([[makeQuery(id+"F20.imprint","IMPRINT",EDGE,{"derivedFrom":sQuery(id+"F20.wireOp",EDGE,"E31.bottom")}),-1.0]])]});
            extrude(context, id + "F21", {"entities" : qUnion([Q0]), "operationType" : NewBodyOperationType.REMOVE, "oppositeDirection" : true, "depth" : 4 * mm, "offsetDistance" : 25 * mm});
        }
        {
            var Q0;
            {var subQ0=sQuery(id+"F2.wireOp",EDGE,"E21.top");var subQ1=sQuery(id+"F2.wireOp",EDGE,"E23.left");Q0=makeQuery(id+"F16.boolean.opBoolean","INTERSECT",EDGE,{"derivedFrom":[makeQuery(id+"F5.boolean.opBoolean","MERGE",FACE,{"derivedFrom":[makeQuery(id+"F3.opExtrude","SWEPT_FACE",FACE,{"disambiguationData":[OSD([sQuery(id+"F1.wireOp",EDGE,"E8.left"),sQuery(id+"F1.wireOp",EDGE,"E20.left")])]}),makeQuery(id+"F5.opExtrude","CAP_FACE",FACE,{"disambiguationData":[OSD([subQ0,sQuery(id+"F2.wireOp",EDGE,"E23.top"),subQ1,sQuery(id+"F2.wireOp",EDGE,"E23.right")])],"isStart":true}),makeQuery(id+"F5.opExtrude","CAP_FACE",FACE,{"disambiguationData":[OSD([subQ0,sQuery(id+"F2.wireOp",EDGE,"E22.top"),sQuery(id+"F2.wireOp",EDGE,"E22.left"),sQuery(id+"F2.wireOp",EDGE,"E22.right")])],"isStart":true})]}),makeQuery(id+"F16.opExtrude","SWEPT_FACE",FACE,{"disambiguationData":[OSD([subQ0]),TDD([makeQuery(id+"F2.imprint","IMPRINT",EDGE,{"disambiguationData":[TD([[makeQuery(id+"F2.imprint","INTERSECT",VERTEX,{"derivedFrom":[subQ0,subQ1]}),-1.0]])],"derivedFrom":subQ0})])]})]});}
            var Q1;
            Q1=makeQuery(id+"F19.boolean.opBoolean","COPY",EDGE,{"derivedFrom":makeQuery(id+"F19.opExtrude","SWEPT_EDGE",EDGE,{"disambiguationData":[OSD([sQuery(id+"F2.wireOp",EDGE,"E21.top"),sQuery(id+"F2.wireOp",EDGE,"E21.left"),sQuery(id+"F2.wireOp",EDGE,"E26.right"),sQuery(id+"F18.wireOp",EDGE,"E30.bottom"),sQuery(id+"F18.wireOp",EDGE,"E30.right")])]})});
            var Q2;
            Q2=makeQuery(id+"F21.boolean.opBoolean","COPY",EDGE,{"derivedFrom":makeQuery(id+"F21.opExtrude","SWEPT_EDGE",EDGE,{"disambiguationData":[OSD([sQuery(id+"F2.wireOp",EDGE,"E21.top"),sQuery(id+"F2.wireOp",EDGE,"E21.right"),sQuery(id+"F2.wireOp",EDGE,"E25.right"),sQuery(id+"F20.wireOp",EDGE,"E31.bottom"),sQuery(id+"F20.wireOp",EDGE,"E31.right")])]})});
            var Q3;
            {var subQ0=sQuery(id+"F2.wireOp",EDGE,"E22.left");var subQ1=sQuery(id+"F2.wireOp",EDGE,"E21.top");Q3=makeQuery(id+"F16.boolean.opBoolean","INTERSECT",EDGE,{"derivedFrom":[makeQuery(id+"F5.boolean.opBoolean","MERGE",FACE,{"derivedFrom":[makeQuery(id+"F3.opExtrude","SWEPT_FACE",FACE,{"disambiguationData":[OSD([sQuery(id+"F1.wireOp",EDGE,"E8.left"),sQuery(id+"F1.wireOp",EDGE,"E20.left")])]}),makeQuery(id+"F5.opExtrude","CAP_FACE",FACE,{"disambiguationData":[OSD([subQ1,sQuery(id+"F2.wireOp",EDGE,"E23.top"),sQuery(id+"F2.wireOp",EDGE,"E23.left"),sQuery(id+"F2.wireOp",EDGE,"E23.right")])],"isStart":true}),makeQuery(id+"F5.opExtrude","CAP_FACE",FACE,{"disambiguationData":[OSD([subQ1,sQuery(id+"F2.wireOp",EDGE,"E22.top"),subQ0,sQuery(id+"F2.wireOp",EDGE,"E22.right")])],"isStart":true})]}),makeQuery(id+"F16.opExtrude","SWEPT_FACE",FACE,{"disambiguationData":[OSD([subQ1]),TDD([makeQuery(id+"F2.imprint","IMPRINT",EDGE,{"disambiguationData":[TD([[makeQuery(id+"F2.imprint","INTERSECT",VERTEX,{"derivedFrom":[subQ1,subQ0]}),1.0]])],"derivedFrom":subQ1})])]})]});}
            fillet(context, id + "F22", {"entities" : qUnion([Q0, Q1, Q2, Q3]), "radius" : 2 * mm, "allowEdgeOverflow" : false});
        }
    });
